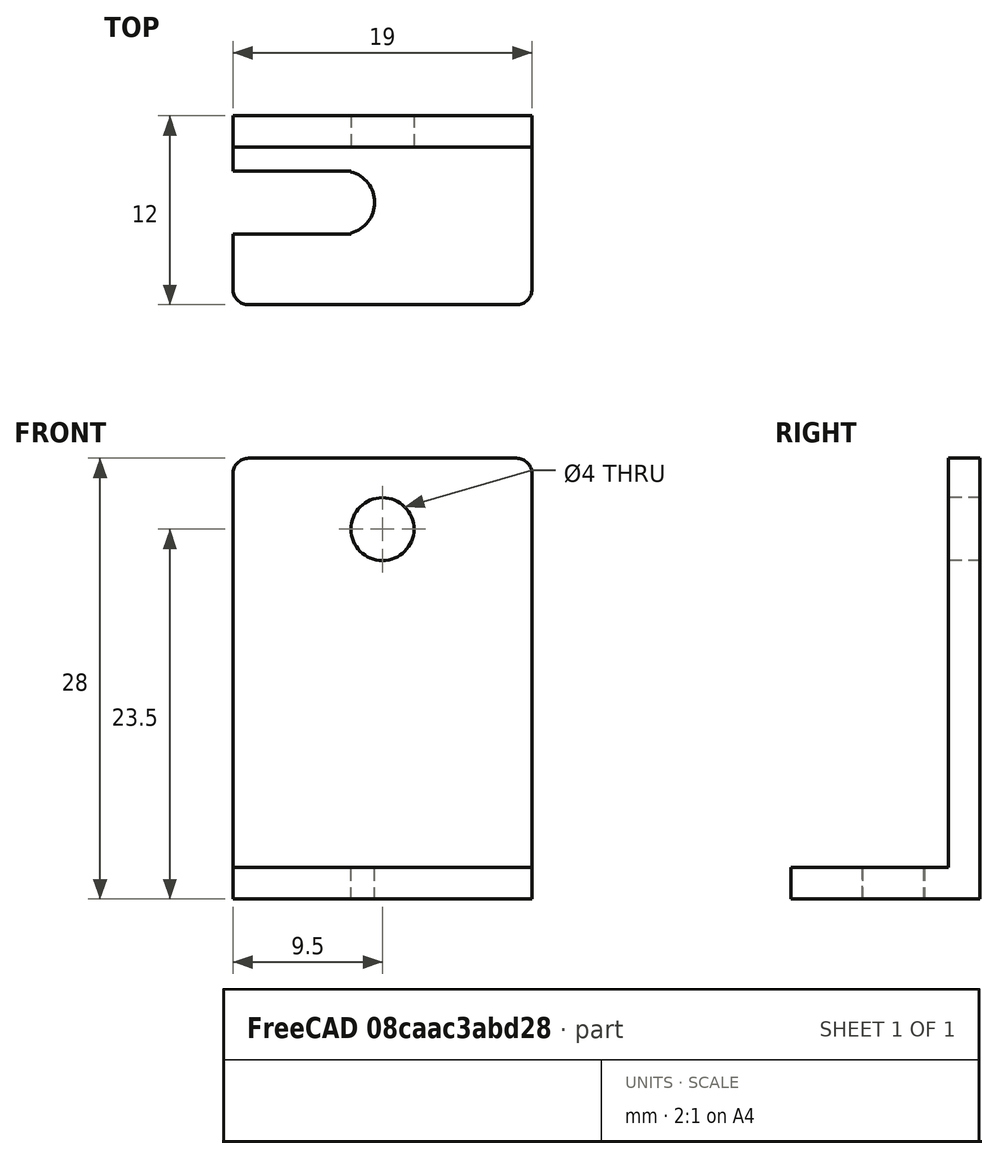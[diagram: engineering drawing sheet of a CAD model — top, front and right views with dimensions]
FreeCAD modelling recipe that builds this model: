
FCSTD DOCUMENT  (FreeCAD 0.18.4R)
Label: COP-Adapter
License: All rights reserved
LicenseURL: http://en.wikipedia.org/wiki/All_rights_reserved
objects: PartDesign::AdditiveBox×2, PartDesign::SubtractiveCylinder×2, PartDesign::SubtractiveBox×1, PartDesign::Fillet×1, PartDesign::Body×1
note: 12 computed .brp shape members not serialized (recipe doc carries the construction recipe); baked Part::Feature solids carry a one-line shape summary decoded from their .brp

FEATURE [PartDesign::AdditiveBox] Box  label="Base"
  AttacherType = Attacher::AttachEngine3D
  AttachmentOffset = pos=(-9.5,-6,0) rot=(0,0,1;0rad)
  Height = 2
  Length = 19
  MapMode = 5
  Placement = pos=(-9.5,-6,0) rot=(0,0,1;0rad)
  Refine = true
  Support = -> [XY_Plane]
  Width = 12
FEATURE [PartDesign::AdditiveBox] Box001  label="Back"
  AttacherType = Attacher::AttachEngine3D
  AttachmentOffset = pos=(0,-9.5,4) rot=(0,0,1;0rad)
  BaseFeature = -> Box
  Height = 2
  Length = 28
  MapMode = 4
  Placement = pos=(-9.5,4,-7e-16) rot=(0.57735,0.57735,0.57735;4.18879rad)
  Refine = true
  Support = -> [YZ_Plane]
  Width = 19
FEATURE [PartDesign::SubtractiveCylinder] Cylinder
  Angle = 360
  AttacherType = Attacher::AttachEngine3D
  AttachmentOffset = pos=(-2.5,0.5,0) rot=(0,0,1;0rad)
  BaseFeature = -> Box001
  Height = 2
  MapMode = 2
  Placement = pos=(-2.5,0.5,0) rot=(0,0,1;0rad)
  Radius = 2
  Refine = true
  Support = -> [XY_Plane]
FEATURE [PartDesign::SubtractiveBox] Box002  label="Hole-Square"
  AttacherType = Attacher::AttachEngine3D
  AttachmentOffset = pos=(-10,-1.5,0) rot=(0,0,1;0rad)
  BaseFeature = -> Cylinder
  Height = 2
  Length = 8
  MapMode = 5
  Placement = pos=(-10,-1.5,0) rot=(0,0,1;0rad)
  Refine = true
  Support = -> [XY_Plane]
  Width = 4
FEATURE [PartDesign::SubtractiveCylinder] Cylinder001
  Angle = 360
  AttacherType = Attacher::AttachEngine3D
  AttachmentOffset = pos=(0,23.5,-6) rot=(0,0,1;0rad)
  BaseFeature = -> Box002
  Height = 2
  MapMode = 5
  Placement = pos=(0,6,23.5) rot=(1,0,0;1.5708rad)
  Radius = 2
  Refine = true
  Support = -> [XZ_Plane]
FEATURE [PartDesign::Fillet] Fillet
  Base = -> Cylinder001 [Edge28,Edge36,Edge33,Edge12]
  BaseFeature = -> Cylinder001
  Placement = pos=(0,6,23.5) rot=(1,0,0;1.5708rad)
  Radius = 1
FEATURE [PartDesign::Body] Body
  Group = -> [Box,Box001,Cylinder,Box002,Cylinder001,Fillet]
  Origin = -> Origin
  Tip = -> Fillet
